# Revit family: EVID-C8.2
name_source: partatom
category: Communication Devices
revit_build: Autodesk Revit 2017 (Build: 20160225_1515(x64)
units: mm (PartAtom-declared; Revit-internal decimal feet)

## family parameters
Always vertical = Yes
Cut with Voids When Loaded = No
Maintain Annotation Orientation = Yes
OmniClass Number = 23.85.10.11.11.21
OmniClass Title = Speakers
Part Type = Normal
Room Calculation Point = No
Round Connector Dimension = Use Diameter
Shared = No
Work Plane-Based = Yes

## types (2) — shared parameters
ArchitectsAndEngineersSpecs = https://www.electrovoice.com
BackLength = 238 mm  [stored 0.78084 ft]
Depth = 294 mm  [stored 0.964567 ft]
Description = 8" coaxial two-way with extended LF. Waveguide coupled Ti Tweeter. Full bandwith overload protection. Front baffle wattage tap adjustment. Integrated low loss matching transformer allows for either 70v/100v or 8-ohm operation. Includes tile bridge and mounting ring for easy installation. Integrated ported enclosure for extended bass reponse.
Disclaimer = http://resource.boschsecurity.com
FrontLength = 300 mm
Height = 294 mm  [stored 0.964567 ft]
IfcExportAs = IfcBuildingElementProxy
IfcExportType = IfcBuildingElementProxyType
InstallationManual = https://www.electrovoice.com
Manufacturer = Electro Voice
ManufacturerURL = https://www.electrovoice.com
MaterialRALColour = RAL9010
PlanningTools = https://www.electrovoice.com
ProductInformation = https://www.electrovoice.com
Uniclass2015Code = Pr_60_75_08_02
Version = 1
zero-valued in all types: Default Elevation

## per-type parameters (varying)
| type | CTN | ModelNumber |
| EVIDC8.2_Ceiling_Speaker_Sys-8In_Pr | EVIDC8.2 | F.01U.117.587 |
| PRD000264100_EVIDC8.2D_Eu_Evac_Compliant_Pair | PRD000264100 | F.01U.139.234 |

note: [stored X ft] marks values corroborated as IEEE doubles in the binary element streams (Revit-internal decimal feet)

## geometry (parser evidence)
native form markers: Blend x2, Sweep x5
no freeform markers — native parametric forms only
